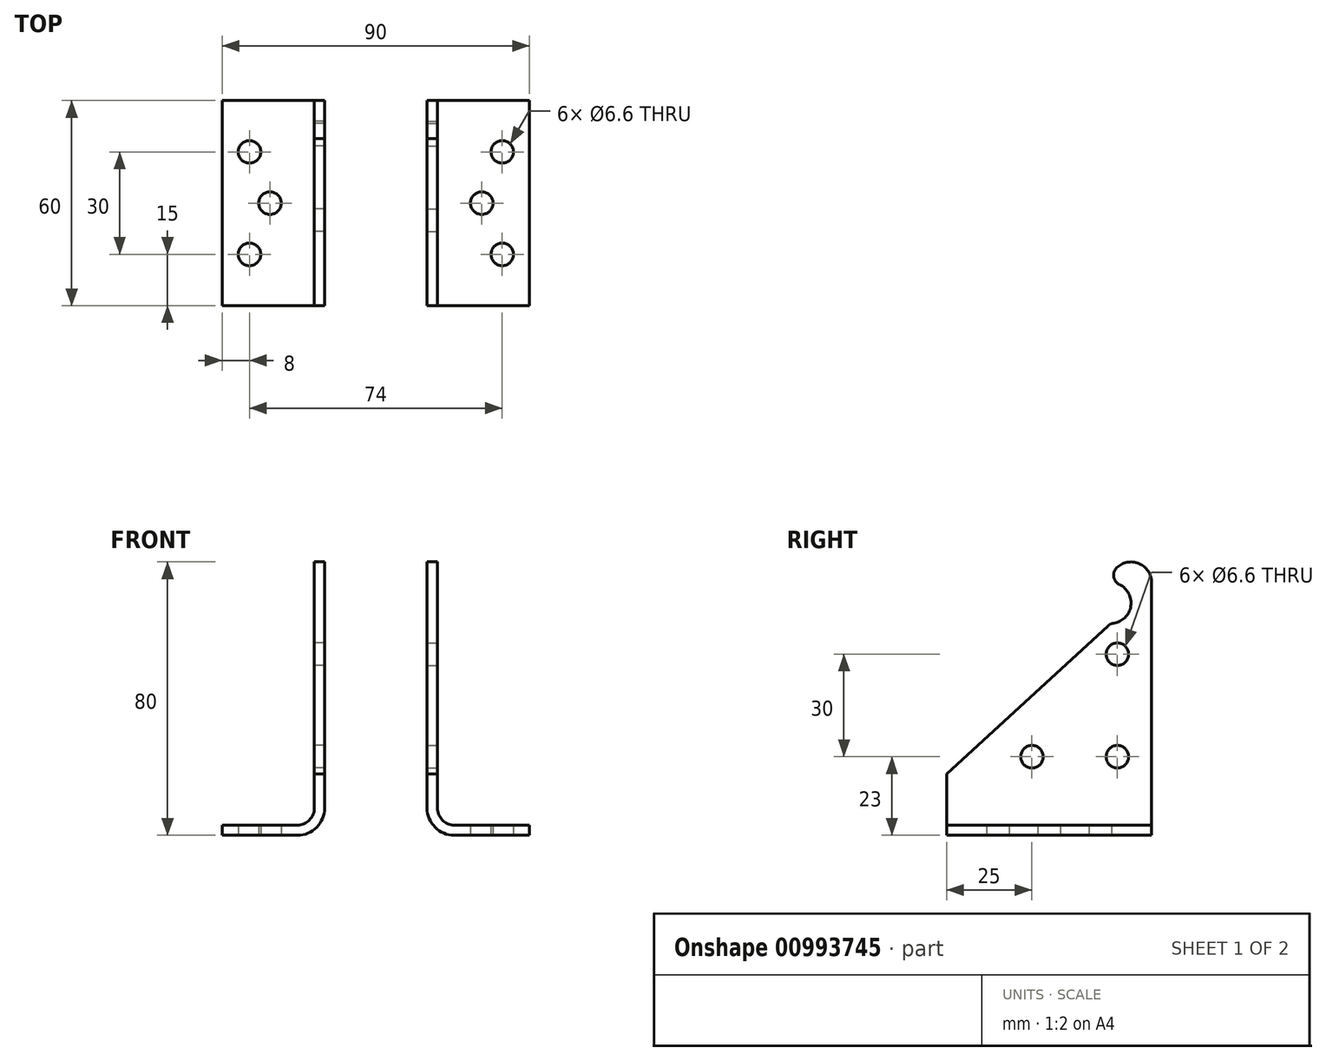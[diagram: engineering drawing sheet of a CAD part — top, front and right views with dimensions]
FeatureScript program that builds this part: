
annotation { "Feature Type Name" : "Feature", "Feature Type Description" : "" }
export const myFeature = defineFeature(function(context is Context, id is Id, definition is map)
    precondition{}
    {
        {
            var Q0;
            Q0=qCreatedBy(makeId("Front.planeOp"),FACE);
            var sketch = newSketch(context, id + "F0", { "sketchPlane" : qUnion([Q0])});
            skLineSegment(sketch, "E0", {"start": v(0, 0) * mm, "end": v(-15, 0) * mm, "construction": true});
            skLineSegment(sketch, "E1", {"start": v(-15, 8) * mm, "end": v(-15, 80) * mm});
            skLineSegment(sketch, "E2", {"start": v(-15, 80) * mm, "end": v(-18, 80) * mm});
            skLineSegment(sketch, "E3", {"start": v(-18, 80) * mm, "end": v(-18, 8) * mm});
            skLineSegment(sketch, "E4", {"start": v(-23, 3) * mm, "end": v(-45, 3) * mm});
            skLineSegment(sketch, "E5", {"start": v(-45, 3) * mm, "end": v(-45, 0) * mm});
            skLineSegment(sketch, "E6", {"start": v(-45, 0) * mm, "end": v(-23, 0) * mm});
            skPoint(sketch, "E7.visualSharp", {"position": v(-18, 3) * mm});
            skArc(sketch, "E7.filletArc", {"start": v(-23, 3) * mm, "mid": v(-19.46, 4.46) * mm, "end": v(-18, 8) * mm});
            skPoint(sketch, "E8.visualSharp", {"position": v(-15, 0) * mm});
            skArc(sketch, "E8.filletArc", {"start": v(-23, 0) * mm, "mid": v(-17.34, 2.34) * mm, "end": v(-15, 8) * mm});
            skSolve(sketch);
        }
        {
            var Q0;
            Q0=makeQuery(id+"F0.imprint","IMPRINT",FACE,{"disambiguationData":[TD([[makeQuery(id+"F0.imprint","IMPRINT",EDGE,{"derivedFrom":sQuery(id+"F0.wireOp",EDGE,"E1")}),1.0]])]});
            extrude(context, id + "F1", {"entities" : qUnion([Q0]), "depth" : 60 * mm, "offsetDistance" : 25 * mm});
        }
        {
            var Q0;
            Q0=makeQuery(id+"F1.opExtrude","SWEPT_FACE",FACE,{"disambiguationData":[OSD([sQuery(id+"F0.wireOp",EDGE,"E3")])]});
            var sketch = newSketch(context, id + "F2", { "sketchPlane" : qUnion([Q0])});
            skLineSegment(sketch, "E9", {"start": v(60, 8) * mm, "end": v(60, 18) * mm, "construction": true});
            skLineSegment(sketch, "E10", {"start": v(60, 80) * mm, "end": v(60, 18) * mm});
            skArc(sketch, "E11", {"start": v(12, 74) * mm, "mid": v(6, 80) * mm, "end": v(0, 74) * mm});
            skLineSegment(sketch, "E12", {"start": v(0, 74) * mm, "end": v(0, 80) * mm});
            skLineSegment(sketch, "E13", {"start": v(0, 80) * mm, "end": v(60, 80) * mm});
            skArc(sketch, "E14", {"start": v(12, 74) * mm, "mid": v(6, 68) * mm, "end": v(12, 62) * mm});
            skLineSegment(sketch, "E15", {"start": v(12, 62) * mm, "end": v(60, 18) * mm});
            skPoint(sketch, "E16", {"position": v(6, 80) * mm});
            skSolve(sketch);
        }
        {
            var Q0;
            Q0=makeQuery(id+"F2.imprint","IMPRINT",FACE,{"disambiguationData":[TD([[makeQuery(id+"F2.imprint","IMPRINT",EDGE,{"derivedFrom":sQuery(id+"F2.wireOp",EDGE,"mrY5R32D-MDwL-qIYa-8F0Q-aZMojLTAYVoU")}),-1.0]])]});
            var Q1;
            {var subQ1=sQuery(id+"F2.wireOp",EDGE,"E10");Q1=makeQuery(id+"F2.imprint","IMPRINT",FACE,{"disambiguationData":[TD([[makeQuery(id+"F2.imprint","IMPRINT",EDGE,{"derivedFrom":subQ1}),-1.0]])]});}
            var Q2;
            {var subQ0=sQuery(id+"F2.wireOp",EDGE,"E12");Q2=makeQuery(id+"F2.imprint","IMPRINT",FACE,{"disambiguationData":[TD([[makeQuery(id+"F2.imprint","IMPRINT",EDGE,{"derivedFrom":subQ0}),1.0]])]});}
            extrude(context, id + "F3", {"entities" : qUnion([Q0, Q1, Q2]), "operationType" : NewBodyOperationType.REMOVE, "oppositeDirection" : true, "depth" : 25 * mm, "offsetDistance" : 25 * mm});
        }
        {
            var Q0;
            Q0=makeQuery(id+"F3.boolean.opBoolean","COPY",EDGE,{"derivedFrom":makeQuery(id+"F3.opExtrude","SWEPT_EDGE",EDGE,{"disambiguationData":[OSD([sQuery(id+"F2.wireOp",EDGE,"E11"),sQuery(id+"F2.wireOp",EDGE,"E14")])]})});
            var Q1;
            Q1=makeQuery(id+"F3.boolean.opBoolean","COPY",EDGE,{"derivedFrom":makeQuery(id+"F3.opExtrude","SWEPT_EDGE",EDGE,{"disambiguationData":[OSD([sQuery(id+"F2.wireOp",EDGE,"E14"),sQuery(id+"F2.wireOp",EDGE,"E15")])]})});
            fillet(context, id + "F4", {"entities" : qUnion([Q0, Q1]), "radius" : 3 * mm, "tangentPropagation" : true, "allowEdgeOverflow" : false});
        }
        {
            var Q0;
            Q0=makeQuery(id+"F1.opExtrude","SWEPT_FACE",FACE,{"disambiguationData":[OSD([sQuery(id+"F0.wireOp",EDGE,"E6")])]});
            var sketch = newSketch(context, id + "F5", { "sketchPlane" : qUnion([Q0])});
            skLineSegment(sketch, "E17.bottom", {"start": v(-23, 60) * mm, "end": v(-45, 60) * mm});
            skLineSegment(sketch, "E17.top", {"start": v(-23, 0) * mm, "end": v(-45, 0) * mm});
            skLineSegment(sketch, "E17.left", {"start": v(-23, 60) * mm, "end": v(-23, 0) * mm});
            skLineSegment(sketch, "E17.right", {"start": v(-45, 60) * mm, "end": v(-45, 0) * mm});
            skLineSegment(sketch, "E18", {"start": v(-34, 60) * mm, "end": v(-34, 0) * mm, "construction": true});
            skCircle(sketch, "E19", {"center": v(-37, 45) * mm, "radius": 3 * mm});
            skCircle(sketch, "E20", {"center": v(-31, 30) * mm, "radius": 3 * mm});
            skCircle(sketch, "E21", {"center": v(-37, 15) * mm, "radius": 3 * mm});
            skPoint(sketch, "E22", {"position": v(-34, 30) * mm});
            skSolve(sketch);
        }
        {
            var Q0;
            Q0=sQuery(id+"F5.wireOp",VERTEX,"E21.center");
            var Q1;
            Q1=sQuery(id+"F5.wireOp",VERTEX,"E20.center");
            var Q2;
            Q2=sQuery(id+"F5.wireOp",VERTEX,"E19.center");
            var Q3;
            Q3=makeQuery(id+"F1.opExtrude","SWEPT_BODY",BODY,{"disambiguationData":[OSD([sQuery(id+"F0.wireOp",EDGE,"E1"),sQuery(id+"F0.wireOp",EDGE,"E2"),sQuery(id+"F0.wireOp",EDGE,"E3"),sQuery(id+"F0.wireOp",EDGE,"E4"),sQuery(id+"F0.wireOp",EDGE,"E5"),sQuery(id+"F0.wireOp",EDGE,"E6"),sQuery(id+"F0.wireOp",EDGE,"E7.filletArc"),sQuery(id+"F0.wireOp",EDGE,"E8.filletArc")])]});
            hole(context, id + "F6", {"style" : HoleStyle.SIMPLE, "endStyle" : HoleEndStyle.THROUGH, "standardTappedOrClearance" : lookupTablePath({ "fit" : "Normal", "standard" : "ISO", "size" : "M6", "type" : "Clearance" }), "standardBlindInLast" : lookupTablePath({ "fit" : "Normal", "standard" : "ISO", "size" : "M6", "type" : "Clearance" }), "holeDiameter" : 6.6 * mm, "majorDiameter" : 5 * mm, "isTappedThrough" : true, "tappedDepth" : 12 * mm, "tapClearance" : 3, "locations" : qUnion([Q0, Q1, Q2]), "scope" : qUnion([Q3])});
        }
        {
            var Q0;
            Q0=makeQuery(id+"F1.opExtrude","SWEPT_FACE",FACE,{"disambiguationData":[OSD([sQuery(id+"F0.wireOp",EDGE,"E3")])]});
            var sketch = newSketch(context, id + "F7", { "sketchPlane" : qUnion([Q0])});
            skLineSegment(sketch, "E23", {"start": v(0, 8) * mm, "end": v(0, 23) * mm, "construction": true});
            skLineSegment(sketch, "E24", {"start": v(0, 23) * mm, "end": v(54.55, 23) * mm, "construction": true});
            skCircle(sketch, "E25", {"center": v(10, 23) * mm, "radius": 4 * mm});
            skCircle(sketch, "E26", {"center": v(35, 23) * mm, "radius": 4 * mm});
            skLineSegment(sketch, "E27", {"start": v(10, 23) * mm, "end": v(10, 62.34) * mm, "construction": true});
            skCircle(sketch, "E28", {"center": v(10, 53) * mm, "radius": 4 * mm});
            skSolve(sketch);
        }
        {
            var Q0;
            Q0=sQuery(id+"F7.wireOp",VERTEX,"E28.center");
            var Q1;
            Q1=sQuery(id+"F7.wireOp",VERTEX,"E27.start");
            var Q2;
            Q2=sQuery(id+"F7.wireOp",VERTEX,"E26.center");
            var Q3;
            Q3=makeQuery(id+"F1.opExtrude","SWEPT_BODY",BODY,{"disambiguationData":[OSD([sQuery(id+"F0.wireOp",EDGE,"E1"),sQuery(id+"F0.wireOp",EDGE,"E2"),sQuery(id+"F0.wireOp",EDGE,"E3"),sQuery(id+"F0.wireOp",EDGE,"E4"),sQuery(id+"F0.wireOp",EDGE,"E5"),sQuery(id+"F0.wireOp",EDGE,"E6"),sQuery(id+"F0.wireOp",EDGE,"E7.filletArc"),sQuery(id+"F0.wireOp",EDGE,"E8.filletArc")])]});
            hole(context, id + "F8", {"style" : HoleStyle.SIMPLE, "endStyle" : HoleEndStyle.THROUGH, "standardTappedOrClearance" : lookupTablePath({ "fit" : "Normal", "standard" : "ISO", "size" : "M6", "type" : "Clearance" }), "standardBlindInLast" : lookupTablePath({ "fit" : "Normal", "standard" : "ISO", "size" : "M6", "type" : "Clearance" }), "holeDiameter" : 6.6 * mm, "majorDiameter" : 5 * mm, "isTappedThrough" : true, "tappedDepth" : 12 * mm, "tapClearance" : 3, "locations" : qUnion([Q0, Q1, Q2]), "scope" : qUnion([Q3])});
        }
        {
            var Q0;
            Q0=makeQuery(id+"F1.opExtrude","SWEPT_BODY",BODY,{"disambiguationData":[OSD([sQuery(id+"F0.wireOp",EDGE,"E1"),sQuery(id+"F0.wireOp",EDGE,"E2"),sQuery(id+"F0.wireOp",EDGE,"E3"),sQuery(id+"F0.wireOp",EDGE,"E4"),sQuery(id+"F0.wireOp",EDGE,"E5"),sQuery(id+"F0.wireOp",EDGE,"E6"),sQuery(id+"F0.wireOp",EDGE,"E7.filletArc"),sQuery(id+"F0.wireOp",EDGE,"E8.filletArc")])]});
            var Q1;
            Q1=qCreatedBy(makeId("Right.planeOp"),FACE);
            mirror(context, id + "F9", {"entities" : qUnion([Q0]), "mirrorPlane" : qUnion([Q1])});
        }
    });
